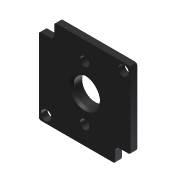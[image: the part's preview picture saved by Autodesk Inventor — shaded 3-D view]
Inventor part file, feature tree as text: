
AUTODESK INVENTOR PART (.ipt)
format: ipt  version: 2013 (Build 170138000, 138)  size: 210,432 bytes
history: native  units: in
note: dims shown in document units (in); Inventor stores cm internally (conversion verified against a paired STEP export)
features: fillet x1, other x1, imported_body x1
ambient origin geometry x8: Origin, YZ Plane, XZ Plane, XY Plane, X Axis, Y Axis, Z Axis, Center Point
feature tree (3):
  fillet  "Fillet4"  [1 undecoded]
  other  "217-2822-BAG Mounting Plate STEP1"
  imported_body  "Base1"
note: 1 required parameter value undecoded (feature->parameter linkage not recoverable at this tier; creation-order binding heuristic only, values carry confidence <= 0.55)
